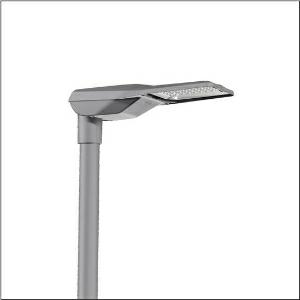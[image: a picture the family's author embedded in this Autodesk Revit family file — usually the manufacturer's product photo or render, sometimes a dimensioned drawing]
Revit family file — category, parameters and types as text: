
# Revit family: streetlight_sl_21_iq_mini___st0_5a_5xe2b31d08jb_7d26
name_source: partatom
category: Lighting Fixtures
units: mm (PartAtom-declared; Revit-internal decimal feet)

## family parameters
Cut with Voids When Loaded = No
Host = Face
Light Source = No
Part Type = Normal
Room Calculation Point = No
Round Connector Dimension = Use Diameter
Shared = No

## types (1)
- --- (1 x LED, 10820 lm, 71.6 W, 3000K)
    Apparent Load = 72 VA
    CIE Flux Codes = 43 76 97 100 100
    Color Rendering = 70
    Color Temperature = 3000K
    Default Elevation = 1800 mm
    Description = Streetlight SL 21 iQ mini, mast luminaire, primary light control with lens, of PMMA, primary optical cover: cover, of toughened safety glass, transparent, light distribution: ST0.5a, light emission: direct distribution, primary light characteristic: asymmetric, installation type: post-top, side-entry, LED, High Power LED, rated luminous flux: 10.820lm, luminous efficacy: 151lm/W, light colour: 730, colour temperature: 3000K, control gear: iQ-Comfort, control: Auto-Match, Temp-Guard, Lumen-Switch, Night-Set, Smart-Wire, Light-Fading, Desk-Remote (wireless, voltage-free reading and setting of iQ features in the workshop via application-optimized NFC function/RFID function), optimised constant luminous flux control (CLO 2.0), pre-setting: linear dimming characteristic, mains connection: 220..240V, AC, 50/60Hz, start of lifetime: 72W, end of service life: 75W, reduction: 33W, luminaire housing, of diecast aluminium, powder-coated, Siteco® metallic grey (DB 702S), corrosivity category C5 mid according to DIN EN ISO 12944, please order mast flange separately, inclination adjustable: 0°, 5°, 10°, 15°, sealing non-destructively replaceable, multi-level sealing system, length: 628mm, width: 235mm, height: 110mm, mast flange for spigot size: 42mm (side-entry): 5XC10008XM4, 60/48mm (side-entry/post-top): 5XC10108XM2, 76/60mm (side-entry/post-top): 5XC10108XM1, mounting height: 4..8m, protection rating (complete): IP66, insulation class (complete): insulation class II (safety insulation), certification: CE, ENEC, ENEC+, VDE, impact resistance: IK10, permissible operating ambient temperature for outdoor applications: -40..+50°C, standard-compliant lighting for roads and squares, packaging unit: 1 piece

Light Distribution: ST0.5a
    Height = 110 mm
    Lamp = 1 x LED
    Lamp Light Flux = 10820 lm
    Lamp Power = 71.6 W
    Lamp count = 1
    Length = 625 mm
    Luminous efficacy = 151 lm/W
    Manufacturer = Siteco
    ModVariant = No
    Model = 5XE2B31D08JB
    Number of Poles = 1
    OnlyDefault = Yes
    Power Factor = 1
    Product Name = Streetlight SL 21 iQ mini | ST0.5a
    Product group = mast luminaire | pylon top
    ProductGroupID = 6100
    Protection Class = Protection class II
    Protection Degree = IP 66
    RLX_Detail_Level = 1
    RLX_Emergency_Light_Flux = 0 lm
    RLX_Emergency_Type = 0
    RLX_Emergency_Type_DB = No
    RlxData = <blob elided: 37565 chars, md5=4771aec6>
    Socket = socket
    Standby Power = 0 W
    System Light Flux = 10820 lm
    System Power = 72 W
    Type Comments = factory setting: luminous flux: 100 % | dim-lin: 254 | 746 mA
    Type Image = l_1003519.jpg
    URL = http://relux.com
    VarID = @adj_193281
    Voltage = 0 V
    Weight = 0.00 kg
    Width = 234 mm

## geometry (parser evidence)
native form markers: Blend x4, Sweep x10
no freeform markers — native parametric forms only
